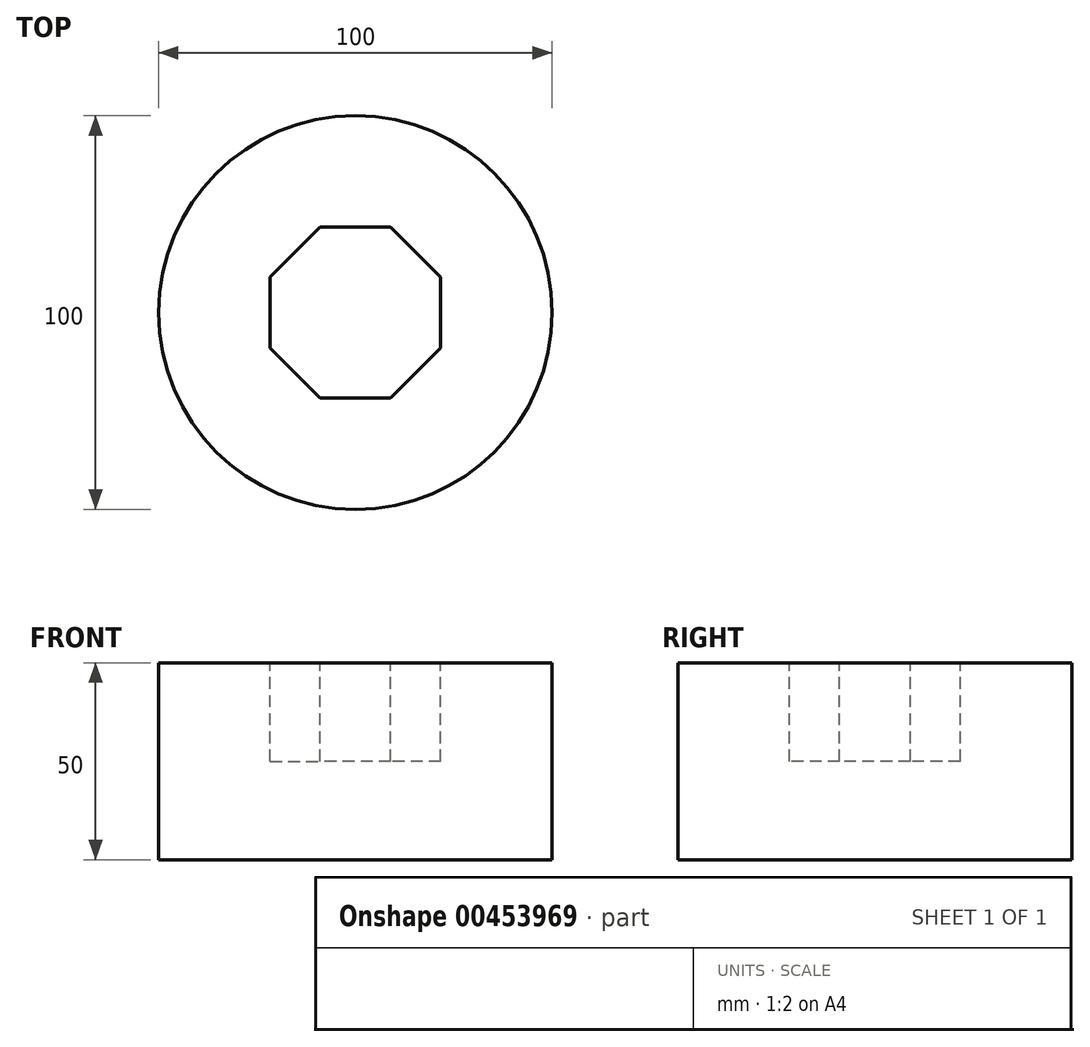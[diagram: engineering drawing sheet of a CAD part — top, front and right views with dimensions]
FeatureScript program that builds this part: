
annotation { "Feature Type Name" : "Feature", "Feature Type Description" : "" }
export const myFeature = defineFeature(function(context is Context, id is Id, definition is map)
    precondition{}
    {
        {
            var Q0;
            Q0=qCreatedBy(makeId("Top.planeOp"),FACE);
            var sketch = newSketch(context, id + "F0", { "sketchPlane" : qUnion([Q0])});
            skCircle(sketch, "E0", {"center": v(0, 0) * mm, "radius": 50 * mm});
            skSolve(sketch);
        }
        {
            var Q0;
            Q0 = qSketchRegion(id + "F0", true);
            extrude(context, id + "F1", {"entities" : qUnion([Q0]), "depth" : 50 * mm});
        }
        {
            var Q0;
            Q0=makeQuery(id+"F1.opExtrude","CAP_FACE",FACE,{"disambiguationData":[OSD([sQuery(id+"F0.wireOp",EDGE,"E0")])],"isStart":false});
            var sketch = newSketch(context, id + "F2", { "sketchPlane" : qUnion([Q0])});
            skCircle(sketch, "E1.cCircle", {"center": v(0, 0) * mm, "radius": 21.69 * mm, "construction": true});
            skLineSegment(sketch, "E1.0", {"start": v(8.98, -21.69) * mm, "end": v(-8.98, -21.69) * mm});
            skLineSegment(sketch, "E1.1", {"start": v(-8.98, -21.69) * mm, "end": v(-21.69, -8.98) * mm});
            skLineSegment(sketch, "E1.2", {"start": v(-21.69, -8.98) * mm, "end": v(-21.69, 8.98) * mm});
            skLineSegment(sketch, "E1.3", {"start": v(-21.69, 8.98) * mm, "end": v(-8.98, 21.69) * mm});
            skLineSegment(sketch, "E1.4", {"start": v(-8.98, 21.69) * mm, "end": v(8.98, 21.69) * mm});
            skLineSegment(sketch, "E1.5", {"start": v(8.98, 21.69) * mm, "end": v(21.69, 8.98) * mm});
            skLineSegment(sketch, "E1.6", {"start": v(21.69, 8.98) * mm, "end": v(21.69, -8.98) * mm});
            skLineSegment(sketch, "E1.7", {"start": v(21.69, -8.98) * mm, "end": v(8.98, -21.69) * mm});
            skPoint(sketch, "E1.0.midPoint", {"position": v(0, -21.69) * mm});
            skSolve(sketch);
        }
        {
            var Q0;
            Q0 = qSketchRegion(id + "F2", true);
            extrude(context, id + "F3", {"entities" : qUnion([Q0]), "operationType" : NewBodyOperationType.REMOVE, "oppositeDirection" : true, "depth" : 25 * mm});
        }
    });
